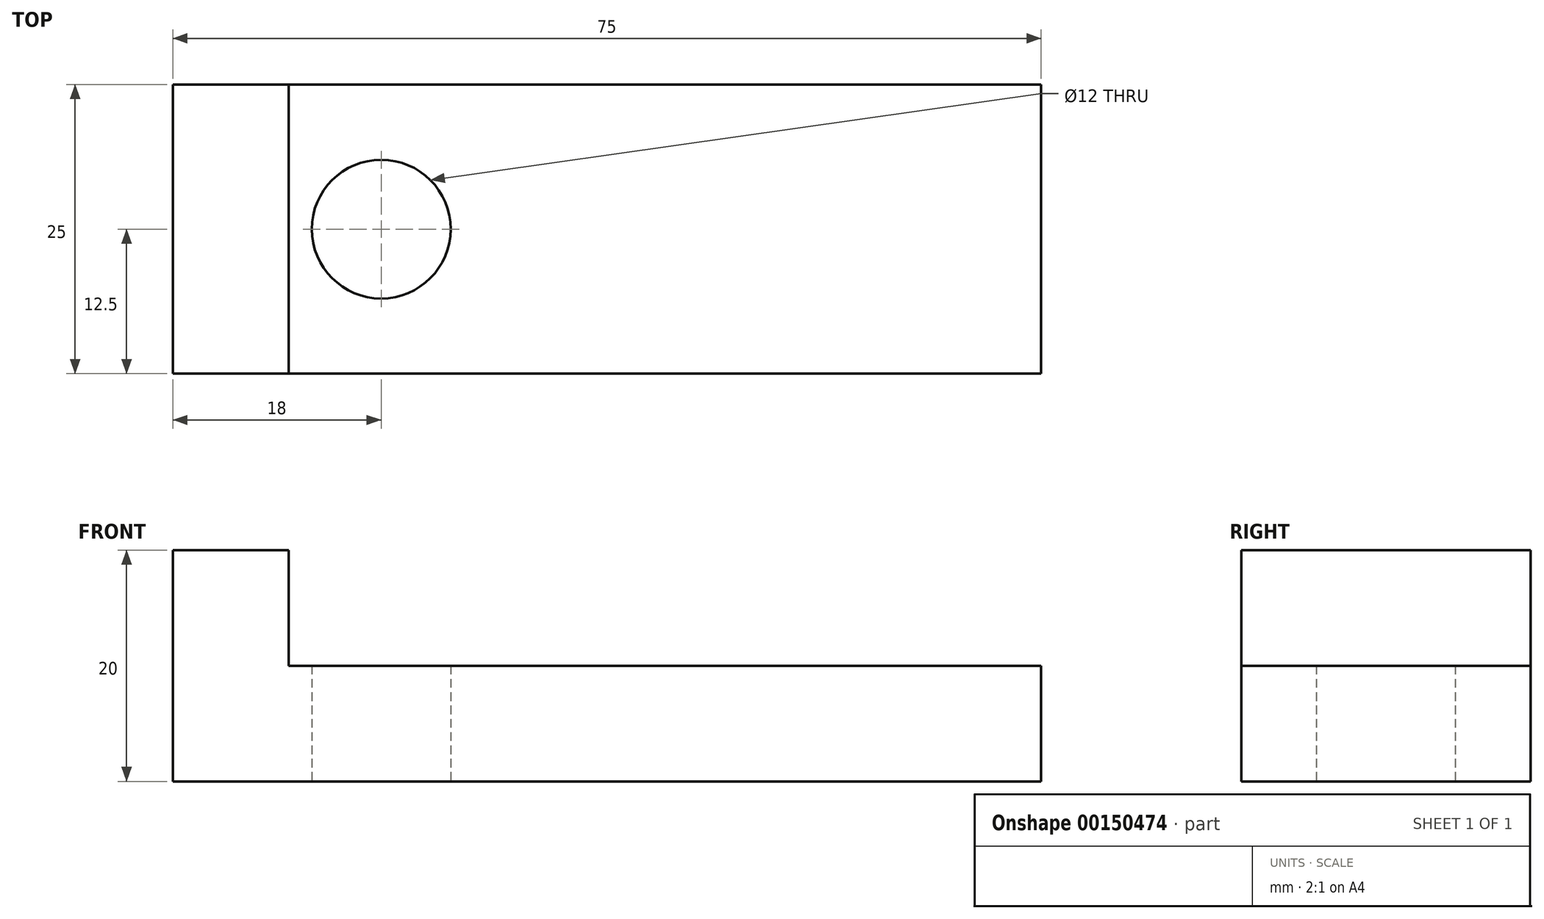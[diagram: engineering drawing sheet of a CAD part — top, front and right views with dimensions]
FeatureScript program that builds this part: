
annotation { "Feature Type Name" : "Feature", "Feature Type Description" : "" }
export const myFeature = defineFeature(function(context is Context, id is Id, definition is map)
    precondition{}
    {
        {
            var Q0;
            Q0=qCreatedBy(makeId("Front.planeOp"),FACE);
            var sketch = newSketch(context, id + "F0", { "sketchPlane" : qUnion([Q0])});
            skLineSegment(sketch, "E0.bottom", {"start": v(0, 0) * mm, "end": v(75, 0) * mm});
            skLineSegment(sketch, "E0.top", {"start": v(10, 10) * mm, "end": v(75, 10) * mm});
            skLineSegment(sketch, "E0.left", {"start": v(0, 0) * mm, "end": v(0, 20) * mm});
            skLineSegment(sketch, "E0.right", {"start": v(75, 0) * mm, "end": v(75, 10) * mm});
            skLineSegment(sketch, "E1", {"start": v(10, 10) * mm, "end": v(10, 20) * mm});
            skLineSegment(sketch, "E2", {"start": v(10, 20) * mm, "end": v(0, 20) * mm});
            skSolve(sketch);
        }
        {
            var Q0;
            Q0=makeQuery(id+"F0.imprint","IMPRINT",FACE,{"disambiguationData":[TD([[makeQuery(id+"F0.imprint","IMPRINT",EDGE,{"derivedFrom":sQuery(id+"F0.wireOp",EDGE,"E0.bottom")}),1.0]])]});
            extrude(context, id + "F1", {"entities" : qUnion([Q0]), "depth" : 25 * mm});
        }
        {
            var Q0;
            Q0=qCreatedBy(makeId("Top.planeOp"),FACE);
            var sketch = newSketch(context, id + "F2", { "sketchPlane" : qUnion([Q0])});
            skCircle(sketch, "E3", {"center": v(18, -12.5) * mm, "radius": 6 * mm});
            skSolve(sketch);
        }
        {
            var Q0;
            Q0=makeQuery(id+"F2.imprint","IMPRINT",FACE,{"disambiguationData":[TD([[makeQuery(id+"F2.imprint","IMPRINT",EDGE,{"derivedFrom":sQuery(id+"F2.wireOp",EDGE,"E3")}),1.0]])]});
            extrude(context, id + "F3", {"entities" : qUnion([Q0]), "operationType" : NewBodyOperationType.REMOVE, "endBound" : BoundingType.THROUGH_ALL, "depth" : 25 * mm});
        }
    });
